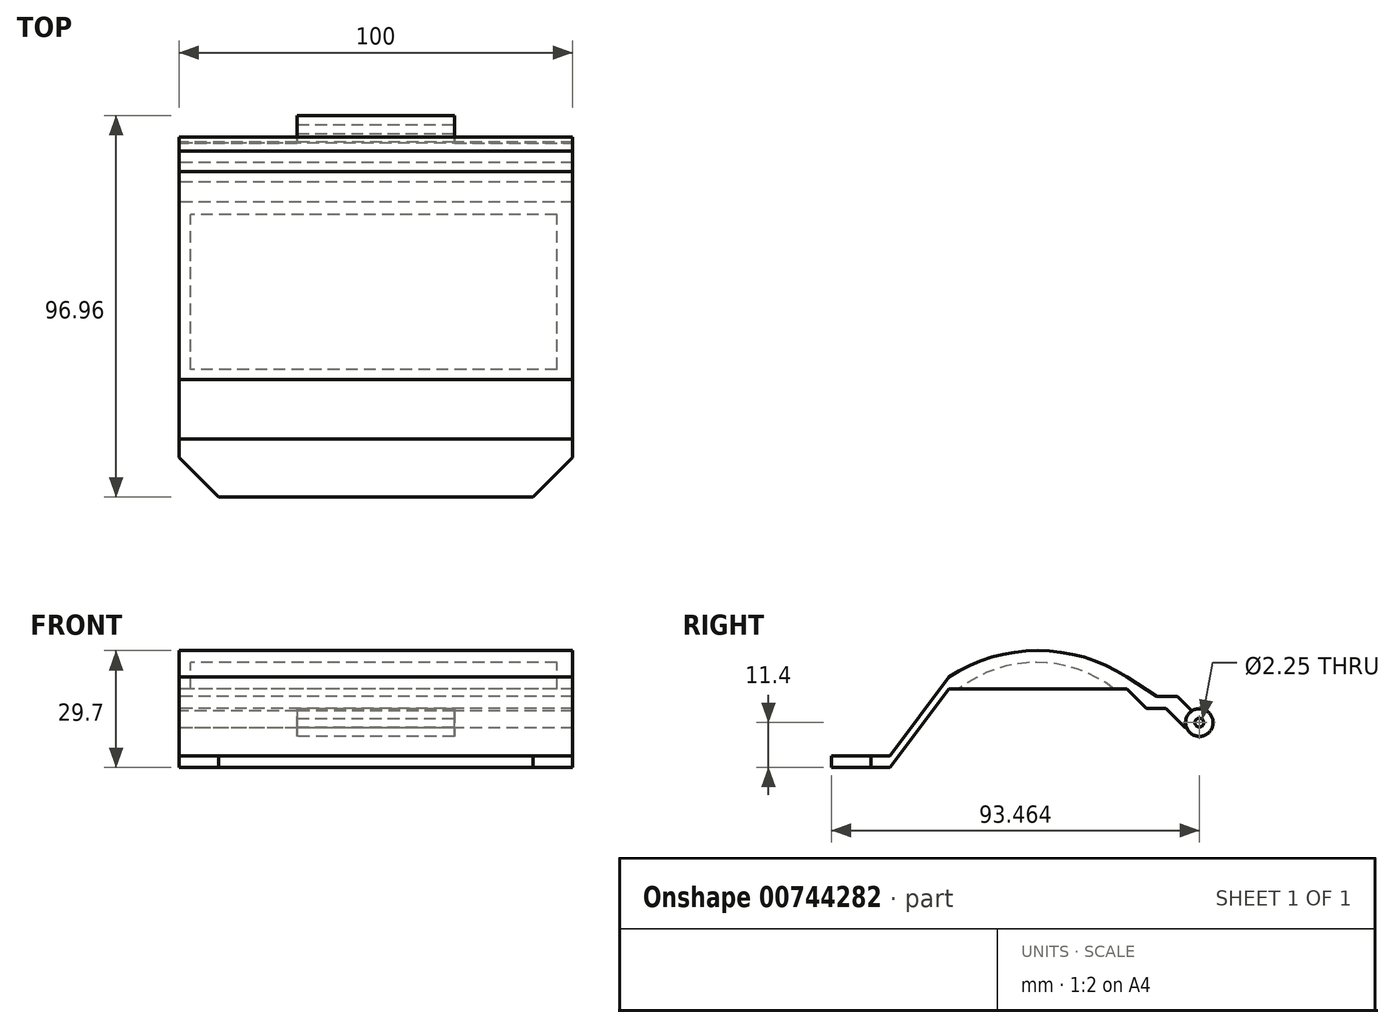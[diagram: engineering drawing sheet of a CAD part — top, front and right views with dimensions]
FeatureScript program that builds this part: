
annotation { "Feature Type Name" : "Feature", "Feature Type Description" : "" }
export const myFeature = defineFeature(function(context is Context, id is Id, definition is map)
    precondition{}
    {
        {
            var Q0;
            Q0=qCreatedBy(makeId("Right.planeOp"),FACE);
            var sketch = newSketch(context, id + "F0", { "sketchPlane" : qUnion([Q0])});
            skArc(sketch, "E0", {"start": v(25.86, -1.4) * mm, "mid": v(32.42, -0.99) * mm, "end": v(27.12, 2.91) * mm});
            skLineSegment(sketch, "E1", {"start": v(25.86, -1.4) * mm, "end": v(25.5, -1.4) * mm});
            skLineSegment(sketch, "E2", {"start": v(25.5, -1.4) * mm, "end": v(20.6, 3.6) * mm});
            skLineSegment(sketch, "E3", {"start": v(27.12, 2.91) * mm, "end": v(23.5, 6.6) * mm});
            skLineSegment(sketch, "E4", {"start": v(23.5, 6.6) * mm, "end": v(18.3, 6.6) * mm});
            skLineSegment(sketch, "E5", {"start": v(20.6, 3.6) * mm, "end": v(15.6, 3.6) * mm});
            skLineSegment(sketch, "E6", {"start": v(15.6, 3.6) * mm, "end": v(10.6, 8.6) * mm});
            skLineSegment(sketch, "E7", {"start": v(18.3, 6.6) * mm, "end": v(10.6, 11.6) * mm});
            skLineSegment(sketch, "E8", {"start": v(10.6, 11.6) * mm, "end": v(-34.59, 11.6) * mm});
            skLineSegment(sketch, "E9", {"start": v(10.6, 8.6) * mm, "end": v(-34.59, 8.6) * mm});
            skLineSegment(sketch, "E10", {"start": v(-34.59, 11.6) * mm, "end": v(-49.59, -8.4) * mm});
            skLineSegment(sketch, "E11", {"start": v(-34.59, 8.6) * mm, "end": v(-49.59, -11.4) * mm});
            skLineSegment(sketch, "E12", {"start": v(-49.59, -11.4) * mm, "end": v(-64.4, -11.4) * mm});
            skLineSegment(sketch, "E13", {"start": v(-64.4, -11.4) * mm, "end": v(-64.4, -8.4) * mm});
            skLineSegment(sketch, "E14", {"start": v(-64.4, -8.4) * mm, "end": v(-49.59, -8.4) * mm});
            skPoint(sketch, "E15.orphan", {"position": v(28.5, 1.5) * mm});
            skArc(sketch, "E16", {"start": v(10.6, 11.6) * mm, "mid": v(-12, 18.3) * mm, "end": v(-34.59, 11.6) * mm});
            skSolve(sketch);
        }
        {
            var Q0;
            Q0=makeQuery(id+"F0.imprint","IMPRINT",FACE,{"disambiguationData":[TD([[makeQuery(id+"F0.imprint","IMPRINT",EDGE,{"derivedFrom":sQuery(id+"F0.wireOp",EDGE,"E0")}),1.0]])]});
            var Q1;
            {var subQ5=sQuery(id+"F0.wireOp",EDGE,"E1");Q1=makeQuery(id+"F0.imprint","IMPRINT",FACE,{"disambiguationData":[TD([[makeQuery(id+"F0.imprint","IMPRINT",EDGE,{"derivedFrom":subQ5}),-1.0]])]});}
            var Q2;
            {var subQ4=sQuery(id+"F0.wireOp",EDGE,"0cY3WKNJ-Mnqc-g7B1-SHFb-kcpAug5wrX5C");Q2=makeQuery(id+"F0.imprint","IMPRINT",FACE,{"disambiguationData":[TD([[makeQuery(id+"F0.imprint","IMPRINT",EDGE,{"derivedFrom":subQ4}),1.0]])]});}
            var Q3;
            Q3=makeQuery(id+"F0.imprint","IMPRINT",FACE,{"disambiguationData":[TD([[makeQuery(id+"F0.imprint","IMPRINT",EDGE,{"derivedFrom":sQuery(id+"F0.wireOp",EDGE,"E8")}),-1.0]])]});
            extrude(context, id + "F1", {"entities" : qUnion([Q0, Q1, Q2, Q3]), "depth" : 100 * mm, "offsetDistance" : 25 * mm});
        }
        {
            var Q0;
            Q0=makeQuery(id+"F1.opExtrude","CAP_EDGE",EDGE,{"disambiguationData":[OSD([sQuery(id+"F0.wireOp",EDGE,"E13")])],"isStart":false});
            var Q1;
            Q1=makeQuery(id+"F1.opExtrude","CAP_EDGE",EDGE,{"disambiguationData":[OSD([sQuery(id+"F0.wireOp",EDGE,"E13")])],"isStart":true});
            chamfer(context, id + "F2", {"entities" : qUnion([Q0, Q1]), "width" : 10 * mm, "tangentPropagation" : true});
        }
        {
            var Q0;
            Q0=makeQuery(id+"F1.opExtrude","CAP_FACE",FACE,{"disambiguationData":[OSD([sQuery(id+"F0.wireOp",EDGE,"E0"),sQuery(id+"F0.wireOp",EDGE,"E1"),sQuery(id+"F0.wireOp",EDGE,"E2"),sQuery(id+"F0.wireOp",EDGE,"E3"),sQuery(id+"F0.wireOp",EDGE,"E4"),sQuery(id+"F0.wireOp",EDGE,"E5"),sQuery(id+"F0.wireOp",EDGE,"E6"),sQuery(id+"F0.wireOp",EDGE,"E7"),sQuery(id+"F0.wireOp",EDGE,"E8"),sQuery(id+"F0.wireOp",EDGE,"E9"),sQuery(id+"F0.wireOp",EDGE,"E10"),sQuery(id+"F0.wireOp",EDGE,"E11"),sQuery(id+"F0.wireOp",EDGE,"E12"),sQuery(id+"F0.wireOp",EDGE,"E13"),sQuery(id+"F0.wireOp",EDGE,"E14")])],"isStart":false});
            var sketch = newSketch(context, id + "F3", { "sketchPlane" : qUnion([Q0])});
            skCircle(sketch, "E17", {"center": v(29.06, 0) * mm, "radius": 3.5 * mm});
            skSolve(sketch);
        }
        {
            var Q0;
            Q0 = qSketchRegion(id + "F3", true);
            extrude(context, id + "F4", {"entities" : qUnion([Q0]), "operationType" : NewBodyOperationType.REMOVE, "oppositeDirection" : true, "depth" : 30 * mm, "offsetDistance" : 25 * mm});
        }
        {
            var Q0;
            Q0=makeQuery(id+"F1.opExtrude","CAP_FACE",FACE,{"disambiguationData":[OSD([sQuery(id+"F0.wireOp",EDGE,"E0"),sQuery(id+"F0.wireOp",EDGE,"E1"),sQuery(id+"F0.wireOp",EDGE,"E2"),sQuery(id+"F0.wireOp",EDGE,"E3"),sQuery(id+"F0.wireOp",EDGE,"E4"),sQuery(id+"F0.wireOp",EDGE,"E5"),sQuery(id+"F0.wireOp",EDGE,"E6"),sQuery(id+"F0.wireOp",EDGE,"E7"),sQuery(id+"F0.wireOp",EDGE,"E8"),sQuery(id+"F0.wireOp",EDGE,"E9"),sQuery(id+"F0.wireOp",EDGE,"E10"),sQuery(id+"F0.wireOp",EDGE,"E11"),sQuery(id+"F0.wireOp",EDGE,"E12"),sQuery(id+"F0.wireOp",EDGE,"E13"),sQuery(id+"F0.wireOp",EDGE,"E14")])],"isStart":true});
            var sketch = newSketch(context, id + "F5", { "sketchPlane" : qUnion([Q0])});
            skCircle(sketch, "E18", {"center": v(-29.06, 0) * mm, "radius": 3.6 * mm});
            skSolve(sketch);
        }
        {
            var Q0;
            Q0 = qSketchRegion(id + "F5", true);
            extrude(context, id + "F6", {"entities" : qUnion([Q0]), "operationType" : NewBodyOperationType.REMOVE, "oppositeDirection" : true, "depth" : 30 * mm, "offsetDistance" : 25 * mm});
        }
        {
            var Q0;
            Q0=makeQuery(id+"F4.boolean.opBoolean","COPY",FACE,{"derivedFrom":makeQuery(id+"F4.opExtrude","CAP_FACE",FACE,{"disambiguationData":[OSD([sQuery(id+"F3.wireOp",EDGE,"E17")])],"isStart":false})});
            var sketch = newSketch(context, id + "F7", { "sketchPlane" : qUnion([Q0])});
            skCircle(sketch, "E19", {"center": v(29.06, 0) * mm, "radius": 1.13 * mm});
            skSolve(sketch);
        }
        {
            var Q0;
            Q0 = qSketchRegion(id + "F7", true);
            extrude(context, id + "F8", {"entities" : qUnion([Q0]), "operationType" : NewBodyOperationType.REMOVE, "endBound" : BoundingType.UP_TO_NEXT, "oppositeDirection" : true, "depth" : 25 * mm, "offsetDistance" : 25 * mm});
        }
        {
            var Q0;
            Q0=makeQuery(id+"F1.opExtrude","CAP_FACE",FACE,{"disambiguationData":[OSD([sQuery(id+"F0.wireOp",EDGE,"E0"),sQuery(id+"F0.wireOp",EDGE,"E1"),sQuery(id+"F0.wireOp",EDGE,"E2"),sQuery(id+"F0.wireOp",EDGE,"E3"),sQuery(id+"F0.wireOp",EDGE,"E4"),sQuery(id+"F0.wireOp",EDGE,"E5"),sQuery(id+"F0.wireOp",EDGE,"E6"),sQuery(id+"F0.wireOp",EDGE,"E7"),sQuery(id+"F0.wireOp",EDGE,"E9"),sQuery(id+"F0.wireOp",EDGE,"E10"),sQuery(id+"F0.wireOp",EDGE,"E11"),sQuery(id+"F0.wireOp",EDGE,"E12"),sQuery(id+"F0.wireOp",EDGE,"E13"),sQuery(id+"F0.wireOp",EDGE,"E14"),sQuery(id+"F0.wireOp",EDGE,"E16")])],"isStart":true});
            cPlane(context, id + "F9", {"entities" : qUnion([Q0]), "cplaneType" : CPlaneType.OFFSET, "offset" : 3 * mm, "oppositeDirection" : true, "width" : 150 * mm, "height" : 150 * mm});
        }
        {
            var Q0;
            Q0=qCreatedBy(id+"F9.planeOp",FACE);
            var sketch = newSketch(context, id + "F10", { "sketchPlane" : qUnion([Q0])});
            skArc(sketch, "E20", {"start": v(32, 8.6) * mm, "mid": v(12.3, 15.3) * mm, "end": v(-7.39, 8.6) * mm});
            skLineSegment(sketch, "E21", {"start": v(32, 8.6) * mm, "end": v(-7.39, 8.6) * mm});
            skSolve(sketch);
        }
        {
            var Q0;
            Q0 = qSketchRegion(id + "F10", true);
            extrude(context, id + "F11", {"entities" : qUnion([Q0]), "operationType" : NewBodyOperationType.REMOVE, "oppositeDirection" : true, "depth" : 93 * mm, "offsetDistance" : 25 * mm});
        }
    });
